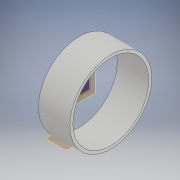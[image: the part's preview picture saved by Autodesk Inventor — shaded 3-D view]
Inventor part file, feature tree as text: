
AUTODESK INVENTOR PART (.ipt)
format: ipt  version: 2019 (Build 230136000, 136)  size: 136,704 bytes
history: native  units: in
note: dims shown in document units (in); Inventor stores cm internally (conversion verified against a paired STEP export)
features: plane x6, sketch x5, extrude x4, projected_geometry x1
ambient origin geometry x8: Origin, YZ Plane, XZ Plane, XY Plane, X Axis, Y Axis, Z Axis, Center Point
bodies: Solid1 (feature_tree)
feature tree (16):
  plane  "Work Plane13"
  sketch  "Sketch6"  dims[d20=0.5315in d47=3.25in]
  plane  "Work Plane14"
  extrude  "Extrusion11"  Depth=3.25in
  plane  "Work Plane10"
  extrude  "Extrusion12"  Depth=0.1in TaperAngle=0.0deg
  plane  "Work Plane9"
  extrude  "Extrusion14"  Depth=1.25in TaperAngle=0.0deg
  extrude  "Extrusion15"  Depth=0.25in TaperAngle=0.0deg
  plane  "Work Plane12"
  plane  "Work Plane11"
  sketch  "Sketch15"  dims[d48=3.5in d49=0.1in d50=0.0in]
  sketch  "Sketch16"  dims[d51=3.25in d52=1.25in d53=0.0in]
  sketch  "Sketch19"  dims[d82=0.25in d83=0.0in d84=0.25in d85=0.0in]
  sketch  "Sketch20"
  projected_geometry  "Projected Loop13"
